# Revit family: ElectricalFixture_WiringAccessories_Hager_Sollysta_SwitchedSockets1Gang
name_source: partatom
category: Electrical Fixtures
revit_build: Autodesk Revit 2015 (Build: 20160512_1515(x64)
units: mm (PartAtom-declared; Revit-internal decimal feet)

## types (2) — shared parameters
CE Approval = Yes
Colour = SollystaWhite
Default Elevation = 1219.2 mm  [stored 4 ft]
Design Country = China
Expected Life = 25 years
Extrusion From Wall = 11.9 mm
Finish = Gloss
Frequency = 50/60Hz
Gross Weight kg = 0.165
Manufacturer = Hager
Manufacturer Country = United Kingdom
Manufacturer Website = http://www.hager.co.uk
Material = Urea Formaldehyde Thermoset Plastic
Overall Depth = 26.1 mm
Overall Height = 86 mm  [stored 0.282152 ft]
Overall Length = 86 mm  [stored 0.282152 ft]
Packaging Recyclable = Yes
Product Family = WhiteMouldedSockets_SwitchedSockets
Product Group = WiringAccessories
Product Literature = http://www.hager.co.uk
Product Range = Sollysta
Product URL = http://www.hager.co.uk
Reference Standard = BS 1363-2
Shape = Rectangular
Shipping Weight kg = 0.188
Supply Phase = 1
Type = ElectricalFixture
Voltage (Volts) = 230V/240V
zero-valued in all types: Overall Width

## per-type parameters (varying)
| type | Description | EAN Code | Features | LED Indicator Switch | Name | Product Model Number | Switch | Technical Description | Unique Reference |
| WMSS81 | 1GangDoublePoleSwitchedSocket | 5015652261100 | 1GangDoublePoleSwitchedSocket | No | WhiteMouldedSocket_WMSS81 | WMSS81 | Yes | 1GangDoublePoleSwitchedSocket | WMSS81 |
| WMSS81 N | 1GangDoublePoleSwitchedSocketWithLEDIndicator | 5015654745448 | 1GangDoublePoleSwitchedSocketWithLEDIndicator | Yes | WhiteMouldedSocket_WMSS81N | WMSS81N | No | 1GangDoublePoleSwitchedSocketWithLEDIndicator | WMSS81N |

note: [stored X ft] marks values corroborated as IEEE doubles in the binary element streams (Revit-internal decimal feet)

## geometry (parser evidence)
native form markers: Blend x4, Sweep x8
no freeform markers — native parametric forms only
